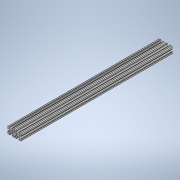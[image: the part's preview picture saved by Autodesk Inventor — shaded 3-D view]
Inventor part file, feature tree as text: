
AUTODESK INVENTOR PART (.ipt)
format: ipt  version: 2020 (Build 240168000, 168)  size: 332,800 bytes
history: native  units: in
note: dims shown in document units (in); Inventor stores cm internally (conversion verified against a paired STEP export)
features: sketch x2, extrude x1
ambient origin geometry x8: Origin, YZ Plane, XZ Plane, XY Plane, X Axis, Y Axis, Z Axis, Center Point
bodies: Solid1 (feature_tree)
feature tree (3):
  extrude  "Extrusion1"  [1 undecoded]
  sketch  "Sketch2"
  sketch  "Sketch1"  dims[d0=22.0in d1=0.0in]
note: 1 required parameter value undecoded (feature->parameter linkage not recoverable at this tier; creation-order binding heuristic only, values carry confidence <= 0.55)
